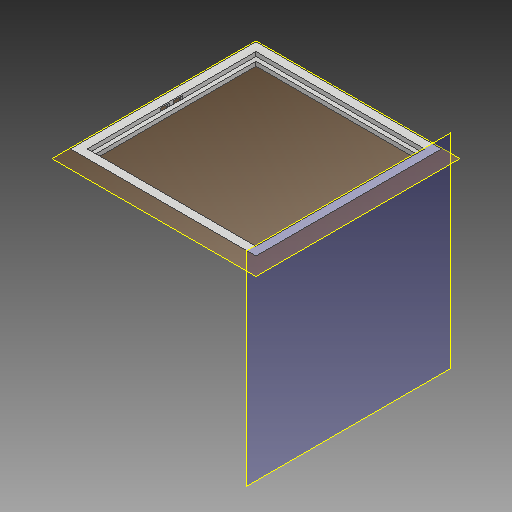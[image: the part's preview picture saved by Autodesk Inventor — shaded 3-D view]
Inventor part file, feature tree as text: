
AUTODESK INVENTOR PART (.ipt)
format: ipt  version: 2018.3 (Build 223284000, 284)  size: 168,960 bytes
history: native  units: mm
features: reference x19, other x10, extrude x4, sketch x4, plane x2, chamfer x1
ambient origin geometry x8: Origin, YZ Plane, XZ Plane, XY Plane, X Axis, Y Axis, Z Axis, Center Point
bodies: Volumenkörper1 (feature_tree)
feature tree (40):
  extrude  "Extrusion1"  Depth=20.0mm TaperAngle=45.0deg
  chamfer  "Fase1"  Distance=17.0mm
  plane  "Arbeitsebene1"
  extrude  "Extrusion2"  Depth=10.0mm
  extrude  "Extrusion3"  Depth=10.0mm
  plane  "Arbeitsebene3"
  extrude  "Extrusion4"  Depth=10.0mm TaperAngle=0.0deg
  sketch  "Skizze1"  dims[d0=20.0mm d1=0.0mm d2=20.0mm d3=2.0mm d4=45.0deg]
  reference  "Referenz1"
  reference  "Referenz2"
  reference  "Referenz3"
  reference  "Referenz4"
  reference  "Referenz5"
  sketch  "Skizze3"  dims[d5=-20.0mm d6=17.0mm d7=0.0mm]
  reference  "Referenz12"
  reference  "Referenz13"
  reference  "Referenz14"
  reference  "Referenz15"
  reference  "Referenz16"
  reference  "Referenz17"
  reference  "Referenz18"
  reference  "Referenz19"
  sketch  "Skizze5"  dims[d8=10.0mm d9=10.0mm]
  sketch  "Skizze6"  dims[d10=10.0mm d11=10.0mm d12=10.0mm d13=0.0mm d14=25.0mm d15=0.0mm]
  reference  "Referenz20"
  reference  "Referenz21"
  reference  "Referenz22"
  reference  "Referenz23"
  reference  "Referenz24"
  reference  "Referenz25"
  parser-record x1  (decoder bookkeeping rows leaked as tree rows — omitted from the tree; the rows remain in map.json)
  other  "SmartCube_Quadratisch.iam"
  other  "Wand2_MIR:1"
  other  "Wand1:1"
  other  "Wand1_MIR:1"
  other  "Wand2:1"
  other  "PV_Modul:1"
  other  "<userpath>\Documents\Dipl\Smartcube_Construction\Version_3\Baugruppe1.iam"
  other  "Baugruppe1.iam"
  other  "PV_Ramen_CPY_3_2:1"
note: 1 file-system path scrubbed to <path> (originals preserved in map.json)
